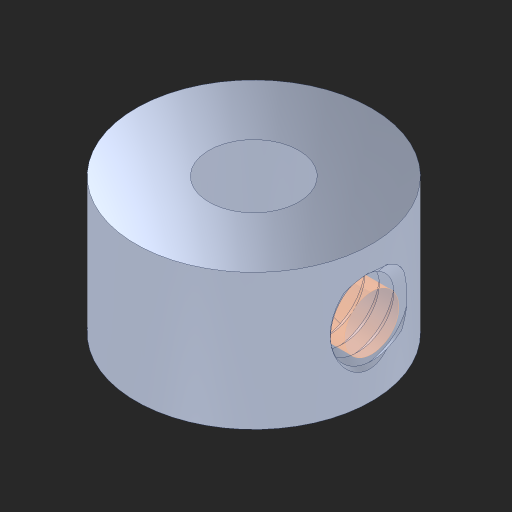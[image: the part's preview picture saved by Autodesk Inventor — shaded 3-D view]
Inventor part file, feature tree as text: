
AUTODESK INVENTOR PART (.ipt)
format: ipt  version: 2023 (Build 270158000, 158)  size: 599,552 bytes
history: native  units: in
note: dims shown in document units (in); Inventor stores cm internally (conversion verified against a paired STEP export)
features: extrude x3, sketch x3, other x2, imported_body x1, plane x1
ambient origin geometry x8: Origin, YZ Plane, XZ Plane, XY Plane, X Axis, Y Axis, Z Axis, Center Point
bodies: Body1 (feature_tree), Body2 (feature_tree)
feature tree (10):
  parser-record x1  (decoder bookkeeping rows leaked as tree rows — omitted from the tree; the rows remain in map.json)
  imported_body  "Base1"
  extrude  "Extrusion1"  Depth=0.005in TaperAngle=0.0deg
  extrude  "Extrusion2"  Depth=1.0in TaperAngle=0.0deg
  plane  "Work Plane1"
  sketch  "Sketch1"  dims[d3=0.005in d4=0.0in d5=0.005in d6=0.0in]
  sketch  "Sketch2"  dims[d7=0.1in d8=1.0in d9=0.0in]
  sketch  "Sketch3"
  other  "Srf1"
  extrude  "ExtrusionSrf1"  [1 undecoded]
note: 1 required parameter value undecoded (feature->parameter linkage not recoverable at this tier; creation-order binding heuristic only, values carry confidence <= 0.55)
